# Revit family: Base_Cabinet-Brown_Jordan-ELEMENTS-Open_Base
name_source: partatom
category: Casework
units: mm (PartAtom-declared; Revit-internal decimal feet)

## family parameters
Always vertical = Yes
Classification Number = 23.40.35.17.47
Cut with Voids When Loaded = No
Room Calculation Point = No
Shared = No
Work Plane-Based = No

## types (4) — shared parameters
Assembly Code = E2010.30
Cabinet Material = Metal - Danver - Stainless Steel
Construction Type = 304 Grade Stainless Steel
Default Elevation = 0' - 0"
Depth = 2' - 3 7/8"
Description = Open Base
Height = 2' - 0 7/8"
Instruction Sheet Link = https://brownjordanoutdoorkitchens.com
Interior Finish = <By Category>
Keynote = 12 31 00
Manufacturer = Brown Jordan Outdoor Kitchens
Product Documentation Link = https://brownjordanoutdoorkitchens.com
Product Name = Open Base
Product Page URL = https://brownjordanoutdoorkitchens.com
URL = https://brownjordanoutdoorkitchens.com
Version = 2019 - V1.0b
Warranty URL = https://brownjordanoutdoorkitchens.com

## per-type parameters (varying)
| type | Constraints | Model | Width |
| 15" Width - 0 Drawers - 0 Doors - 28" Depth | 1 | ELEM OBO1500 | 1' - 3" |
| 18" Width - 0 Drawers - 0 Doors - 28" Depth | 2 | ELEM OBO1800 | 1' - 6" |
| 24" Width - 0 Drawers - 0 Doors - 28" Depth | 3 | ELEM OBO2400 | 2' - 0" |
| 30" Width - 0 Drawers - 0 Doors - 28" Depth | 4 | ELEM OBO3000 | 2' - 6" |

## geometry (parser evidence)
native form markers: Sweep x5
no freeform markers — native parametric forms only
